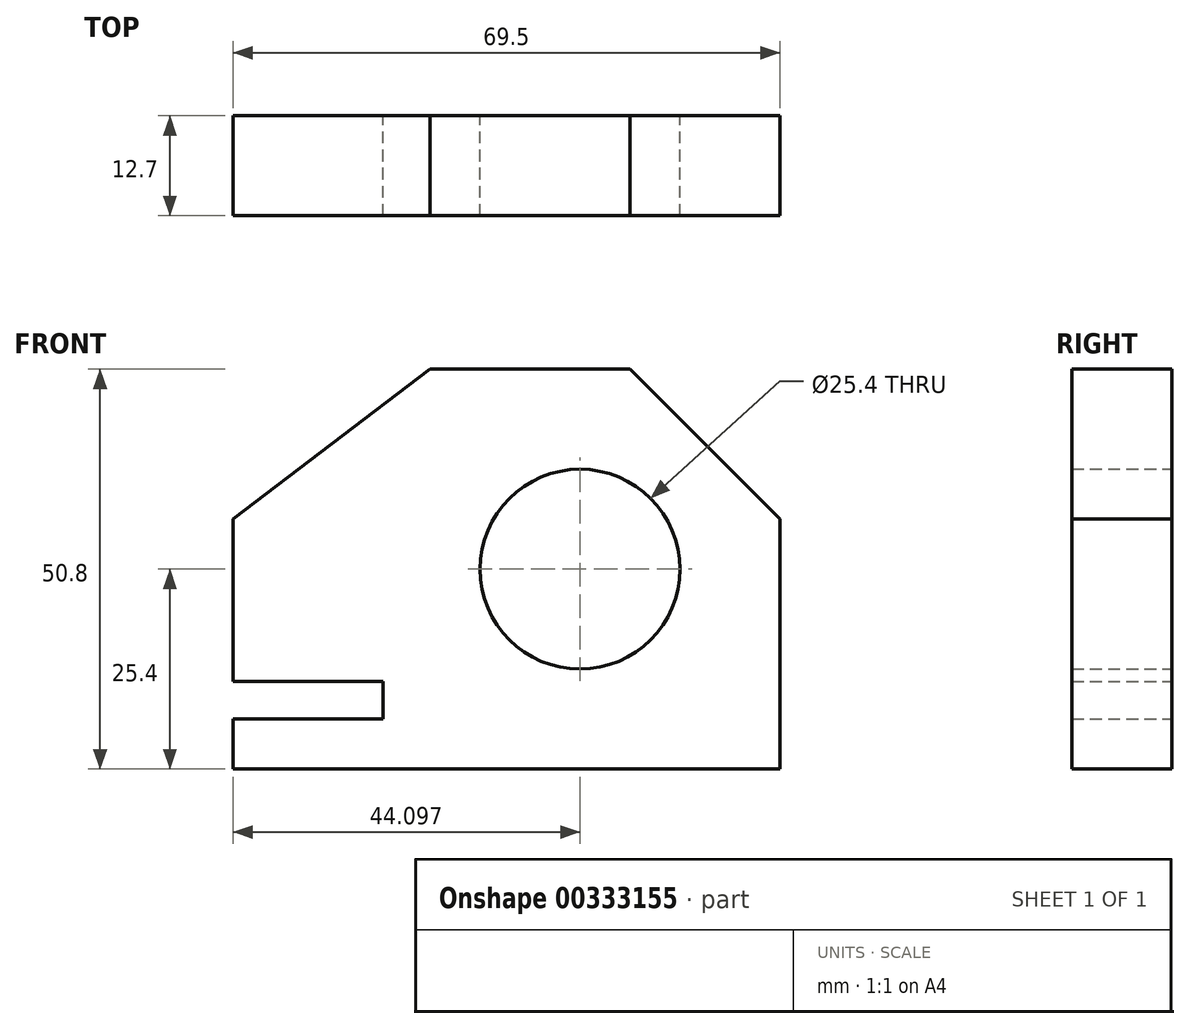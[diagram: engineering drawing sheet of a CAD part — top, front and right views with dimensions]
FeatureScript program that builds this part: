
annotation { "Feature Type Name" : "Feature", "Feature Type Description" : "" }
export const myFeature = defineFeature(function(context is Context, id is Id, definition is map)
    precondition{}
    {
        {
            var Q0;
            Q0=qCreatedBy(makeId("Front.planeOp"),FACE);
            var sketch = newSketch(context, id + "F0", { "sketchPlane" : qUnion([Q0])});
            skLineSegment(sketch, "E0", {"start": v(0, 0) * mm, "end": v(0, 6.35) * mm});
            skLineSegment(sketch, "E1", {"start": v(0, 6.35) * mm, "end": v(19.05, 6.35) * mm});
            skLineSegment(sketch, "E2", {"start": v(19.05, 6.35) * mm, "end": v(19.05, 11.15) * mm});
            skLineSegment(sketch, "E3", {"start": v(19.05, 11.15) * mm, "end": v(0, 11.15) * mm});
            skLineSegment(sketch, "E4", {"start": v(0, 11.15) * mm, "end": v(0, 31.75) * mm});
            skLineSegment(sketch, "E5", {"start": v(0, 31.75) * mm, "end": v(25.05, 50.8) * mm});
            skLineSegment(sketch, "E6", {"start": v(25.05, 50.8) * mm, "end": v(50.45, 50.8) * mm});
            skLineSegment(sketch, "E7", {"start": v(50.45, 50.8) * mm, "end": v(69.5, 31.75) * mm});
            skLineSegment(sketch, "E8", {"start": v(69.5, 31.75) * mm, "end": v(69.5, 0) * mm});
            skLineSegment(sketch, "E9", {"start": v(69.5, 0) * mm, "end": v(0, 0) * mm});
            skCircle(sketch, "E10", {"center": v(44.1, 25.4) * mm, "radius": 12.7 * mm});
            skSolve(sketch);
        }
        {
            var Q0;
            Q0 = qSketchRegion(id + "F0", true);
            extrude(context, id + "F1", {"entities" : qUnion([Q0]), "depth" : 12.7 * mm});
        }
    });
